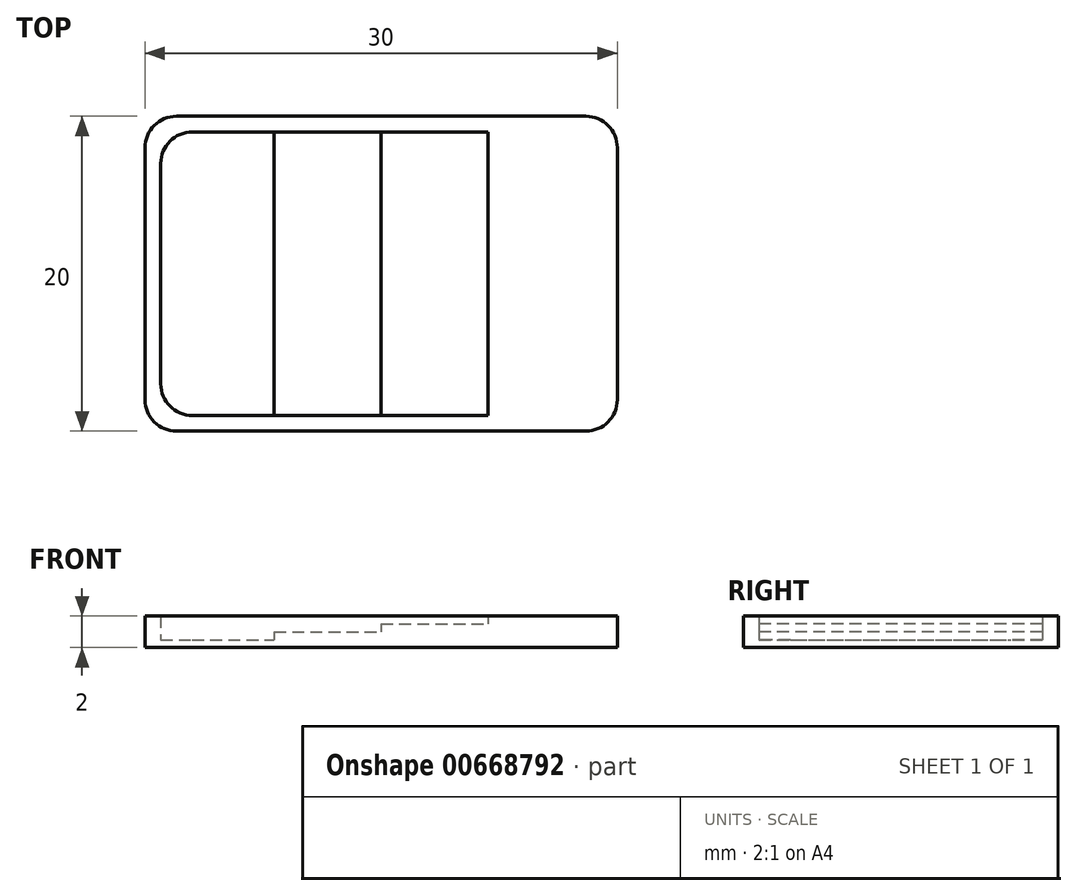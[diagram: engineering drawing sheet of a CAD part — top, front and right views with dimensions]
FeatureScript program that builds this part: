
annotation { "Feature Type Name" : "Feature", "Feature Type Description" : "" }
export const myFeature = defineFeature(function(context is Context, id is Id, definition is map)
    precondition{}
    {
        {
            var Q0;
            Q0=qCreatedBy(makeId("Top.planeOp"),FACE);
            var sketch = newSketch(context, id + "F0", { "sketchPlane" : qUnion([Q0])});
            skLineSegment(sketch, "E0.bottom", {"start": v(-13, -10) * mm, "end": v(13, -10) * mm});
            skLineSegment(sketch, "E0.top", {"start": v(-13, 10) * mm, "end": v(13, 10) * mm});
            skLineSegment(sketch, "E0.left", {"start": v(-15, -8) * mm, "end": v(-15, 8) * mm});
            skLineSegment(sketch, "E0.right", {"start": v(15, -8) * mm, "end": v(15, 8) * mm});
            skPoint(sketch, "E0.middle", {"position": v(0, 0) * mm});
            skLineSegment(sketch, "E1.0", {"start": v(-12, 9) * mm, "end": v(12, 9) * mm});
            skLineSegment(sketch, "E1.1", {"start": v(-14, -7) * mm, "end": v(-14, 7) * mm});
            skLineSegment(sketch, "E1.2", {"start": v(-12, -9) * mm, "end": v(12, -9) * mm});
            skLineSegment(sketch, "E1.3", {"start": v(14, -7) * mm, "end": v(14, 7) * mm});
            skLineSegment(sketch, "E2", {"start": v(0, 9) * mm, "end": v(0, -9) * mm});
            skPoint(sketch, "E3.visualSharp", {"position": v(-15, 10) * mm});
            skArc(sketch, "E3.filletArc", {"start": v(-13, 10) * mm, "mid": v(-14.41, 9.41) * mm, "end": v(-15, 8) * mm});
            skPoint(sketch, "E4.visualSharp", {"position": v(-14, 9) * mm});
            skArc(sketch, "E4.filletArc", {"start": v(-12, 9) * mm, "mid": v(-13.41, 8.41) * mm, "end": v(-14, 7) * mm});
            skPoint(sketch, "E5.visualSharp", {"position": v(14, 9) * mm});
            skArc(sketch, "E5.filletArc", {"start": v(14, 7) * mm, "mid": v(13.41, 8.41) * mm, "end": v(12, 9) * mm});
            skPoint(sketch, "E6.visualSharp", {"position": v(15, 10) * mm});
            skArc(sketch, "E6.filletArc", {"start": v(15, 8) * mm, "mid": v(14.41, 9.41) * mm, "end": v(13, 10) * mm});
            skPoint(sketch, "E7.visualSharp", {"position": v(-14, -9) * mm});
            skArc(sketch, "E7.filletArc", {"start": v(-14, -7) * mm, "mid": v(-13.41, -8.41) * mm, "end": v(-12, -9) * mm});
            skPoint(sketch, "E8.visualSharp", {"position": v(-15, -10) * mm});
            skArc(sketch, "E8.filletArc", {"start": v(-15, -8) * mm, "mid": v(-14.41, -9.41) * mm, "end": v(-13, -10) * mm});
            skPoint(sketch, "E9.visualSharp", {"position": v(15, -10) * mm});
            skArc(sketch, "E9.filletArc", {"start": v(13, -10) * mm, "mid": v(14.41, -9.41) * mm, "end": v(15, -8) * mm});
            skPoint(sketch, "E10.visualSharp", {"position": v(14, -9) * mm});
            skArc(sketch, "E10.filletArc", {"start": v(12, -9) * mm, "mid": v(13.41, -8.41) * mm, "end": v(14, -7) * mm});
            skLineSegment(sketch, "E11", {"start": v(0, 0) * mm, "end": v(-14, 0) * mm, "construction": true});
            skLineSegment(sketch, "E12", {"start": v(-6.8, -9) * mm, "end": v(-6.8, 9) * mm});
            skLineSegment(sketch, "E13.MirrorCS", {"start": v(6.8, -9) * mm, "end": v(6.8, 9) * mm});
            skSolve(sketch);
        }
        {
            var Q0;
            Q0=makeQuery(id+"F0.imprint","IMPRINT",FACE,{"disambiguationData":[TD([[makeQuery(id+"F0.imprint","IMPRINT",EDGE,{"derivedFrom":sQuery(id+"F0.wireOp",EDGE,"E0.bottom")}),1.0]])]});
            extrude(context, id + "F1", {"entities" : qUnion([Q0]), "depth" : 2 * mm, "offsetDistance" : 25 * mm});
        }
        {
            var Q0;
            Q0=makeQuery(id+"F0.imprint","IMPRINT",FACE,{"disambiguationData":[TD([[makeQuery(id+"F0.imprint","IMPRINT",EDGE,{"derivedFrom":sQuery(id+"F0.wireOp",EDGE,"E1.1")}),-1.0]])]});
            extrude(context, id + "F2", {"entities" : qUnion([Q0]), "operationType" : NewBodyOperationType.ADD, "depth" : .5 * mm, "offsetDistance" : 25 * mm});
        }
        {
            var Q0;
            {var subQ0=sQuery(id+"F0.wireOp",EDGE,"E2");Q0=makeQuery(id+"F0.imprint","IMPRINT",FACE,{"disambiguationData":[TD([[makeQuery(id+"F0.imprint","IMPRINT",EDGE,{"derivedFrom":subQ0}),1.0]])]});}
            extrude(context, id + "F3", {"entities" : qUnion([Q0]), "operationType" : NewBodyOperationType.ADD, "depth" : 1.5 * mm, "offsetDistance" : 25 * mm});
        }
        {
            var Q0;
            {var subQ0=sQuery(id+"F0.wireOp",EDGE,"E2");Q0=makeQuery(id+"F0.imprint","IMPRINT",FACE,{"disambiguationData":[TD([[makeQuery(id+"F0.imprint","IMPRINT",EDGE,{"derivedFrom":subQ0}),-1.0]])]});}
            extrude(context, id + "F4", {"entities" : qUnion([Q0]), "operationType" : NewBodyOperationType.ADD, "depth" : 1 * mm, "offsetDistance" : 25 * mm});
        }
        {
            var Q0;
            Q0=makeQuery(id+"F0.imprint","IMPRINT",FACE,{"disambiguationData":[TD([[makeQuery(id+"F0.imprint","IMPRINT",EDGE,{"derivedFrom":sQuery(id+"F0.wireOp",EDGE,"E1.3")}),1.0]])]});
            extrude(context, id + "F5", {"entities" : qUnion([Q0]), "operationType" : NewBodyOperationType.ADD, "depth" : 2 * mm, "offsetDistance" : 25 * mm});
        }
    });
